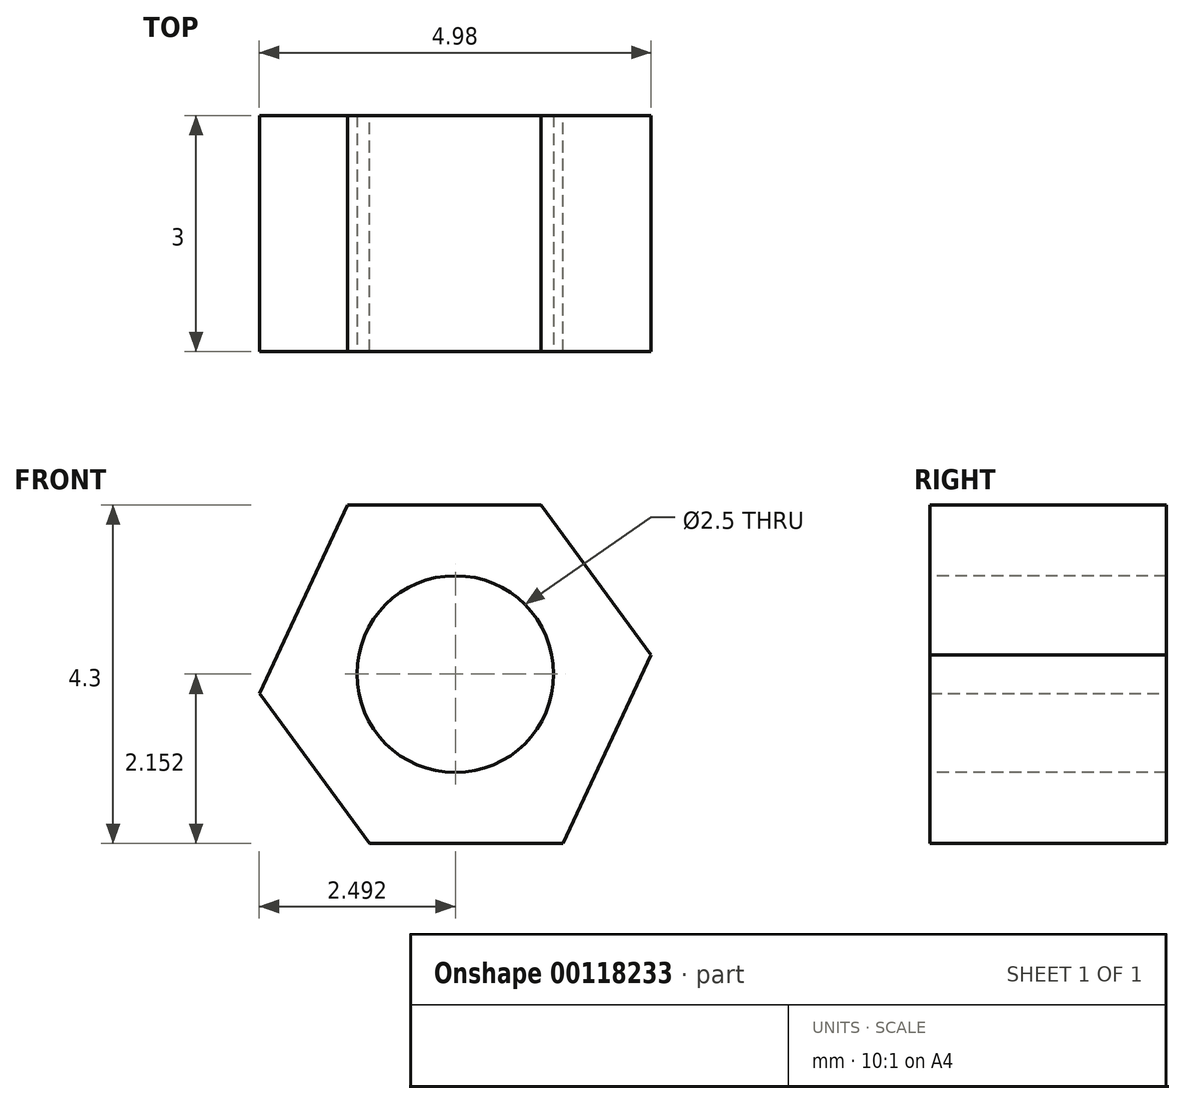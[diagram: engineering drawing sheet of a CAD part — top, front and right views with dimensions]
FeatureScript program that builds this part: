
annotation { "Feature Type Name" : "Feature", "Feature Type Description" : "" }
export const myFeature = defineFeature(function(context is Context, id is Id, definition is map)
    precondition{}
    {
        {
            var Q0;
            Q0=qCreatedBy(makeId("Front.planeOp"),FACE);
            var sketch = newSketch(context, id + "F0", { "sketchPlane" : qUnion([Q0])});
            skLineSegment(sketch, "E0", {"start": v(-0.33, 29.88) * mm, "end": v(2.13, 29.88) * mm});
            skLineSegment(sketch, "E1", {"start": v(2.13, 29.88) * mm, "end": v(3.53, 27.97) * mm});
            skLineSegment(sketch, "E2", {"start": v(3.53, 27.97) * mm, "end": v(2.4, 25.58) * mm});
            skLineSegment(sketch, "E3", {"start": v(2.4, 25.58) * mm, "end": v(-0.05, 25.58) * mm});
            skLineSegment(sketch, "E4", {"start": v(-0.05, 25.58) * mm, "end": v(-1.45, 27.49) * mm});
            skLineSegment(sketch, "E5", {"start": v(-1.45, 27.49) * mm, "end": v(-0.33, 29.88) * mm});
            skSolve(sketch);
        }
        {
            var Q0;
            Q0 = qSketchRegion(id + "F0", true);
            extrude(context, id + "F1", {"entities" : qUnion([Q0]), "depth" : 3 * mm});
        }
        {
            var Q0;
            Q0=makeQuery(id+"F1.opExtrude","CAP_FACE",FACE,{"disambiguationData":[OSD([sQuery(id+"F0.wireOp",EDGE,"E0"),sQuery(id+"F0.wireOp",EDGE,"E1"),sQuery(id+"F0.wireOp",EDGE,"E2"),sQuery(id+"F0.wireOp",EDGE,"E3"),sQuery(id+"F0.wireOp",EDGE,"E4"),sQuery(id+"F0.wireOp",EDGE,"E5")])],"isStart":false});
            var sketch = newSketch(context, id + "F2", { "sketchPlane" : qUnion([Q0])});
            skPoint(sketch, "E6", {"position": v(1.04, 27.73) * mm});
            skCircle(sketch, "E7", {"center": v(1.04, 27.73) * mm, "radius": 1.25 * mm});
            skSolve(sketch);
        }
        {
            var Q0;
            Q0 = qSketchRegion(id + "F2", true);
            extrude(context, id + "F3", {"entities" : qUnion([Q0]), "operationType" : NewBodyOperationType.REMOVE, "oppositeDirection" : true, "depth" : 25 * mm});
        }
    });
